# Revit family: 1035R
name_source: partatom
category: Plumbing Fixtures
revit_build: Autodesk Revit 2018 (Build: 20170223_1515(x64)
units: mm (PartAtom-declared; Revit-internal decimal feet)

## family parameters
Cut with Voids When Loaded = No
Host = Face
OmniClass Number = 23.45.05.21.11.21
OmniClass Title = Urinals
Part Type = Normal
Room Calculation Point = No
Round Connector Dimension = Use Diameter
Shared = Yes

## types (1)
- 1035R
    1035R Rear Mount Urinal, HEU, Wall Supply = Yes
    Assembly Code = D2010210
    CW Connection = Yes
    CWFU = 5
    Connection Size = 1 1/2"
    Default Elevation = 20"
    Description = Urinal Rear Mounted High-Efficiency Washout Urinal
    EG Enviro-Glaze (for color selection see flier) = No
    Flow Rate = 1/8 GPF (0.47 Liters per Flush)
    HW Connection = No
    HWFU = 0
    Height = 22 3/4"
    Inlet Diameter Connection = 3/4"
    Length = 17"
    Manufacturer = Murdockmfg
    Material = 14 gage, type 304 Stainless steel
    Model = 1035R
    Product Documentation Link = https://www.murdockmfg.com
    Product URL = https://www.murdockmfg.com
    URL = https://www.murdockmfg.com
    Vent Connection = No
    WFU = 5
    Warranty Documentation Link = https://www.murdockmfg.com
    Waste Connection = Yes
    Width = 13"

## geometry (parser evidence)
native form markers: Sweep x2
no freeform markers — native parametric forms only
